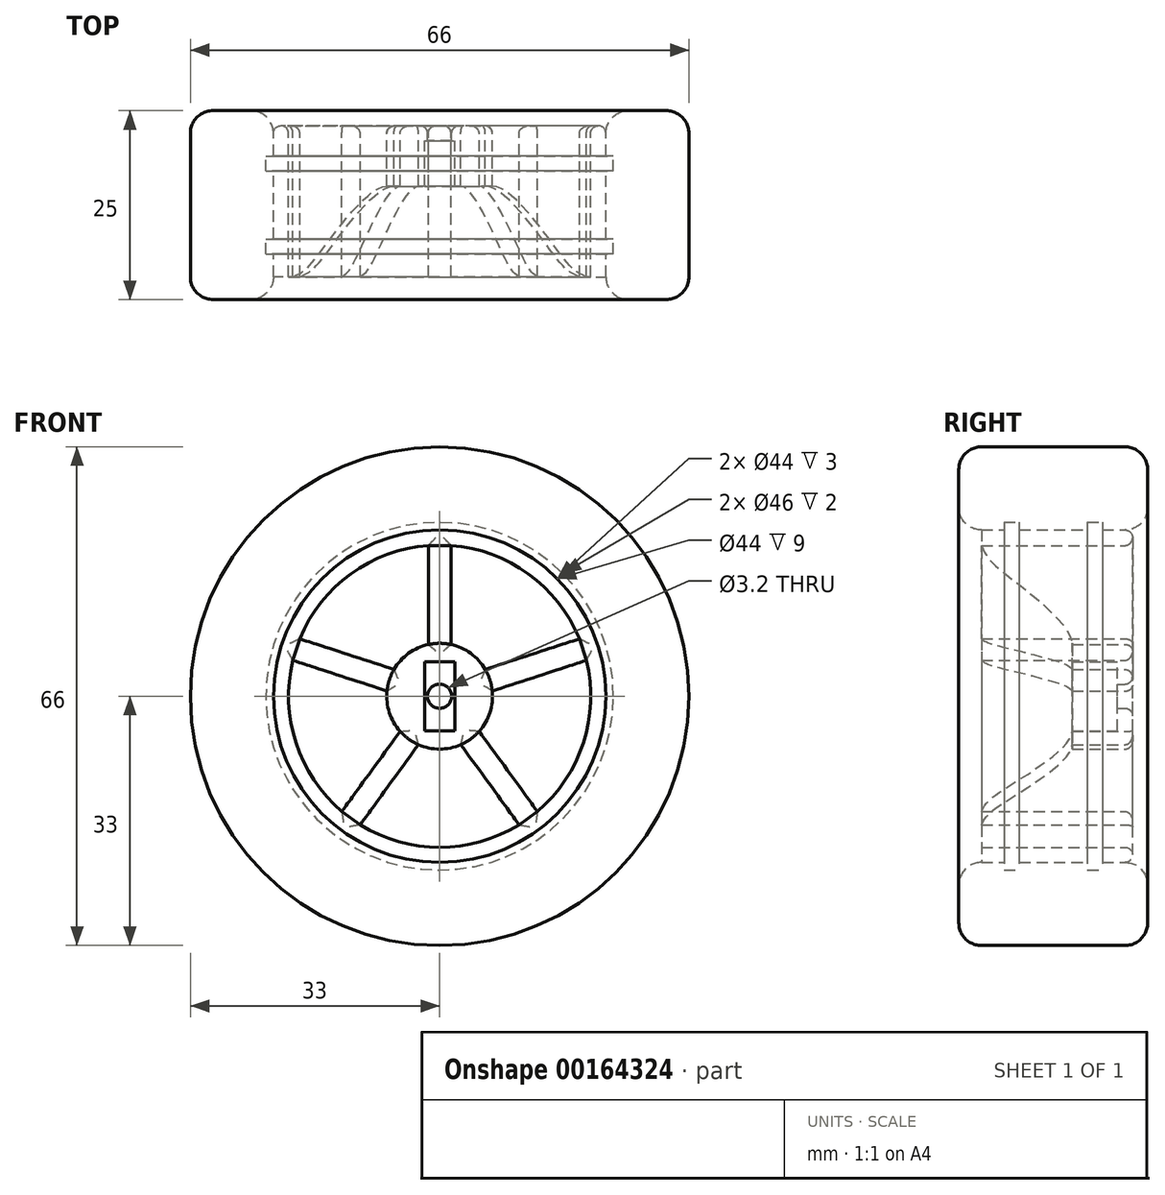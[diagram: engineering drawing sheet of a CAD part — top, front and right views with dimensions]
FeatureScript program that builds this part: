
annotation { "Feature Type Name" : "Feature", "Feature Type Description" : "" }
export const myFeature = defineFeature(function(context is Context, id is Id, definition is map)
    precondition{}
    {
        {
            var Q0;
            Q0=qCreatedBy(makeId("Front.planeOp"),FACE);
            var sketch = newSketch(context, id + "F0", { "sketchPlane" : qUnion([Q0])});
            skCircle(sketch, "E0", {"center": v(0, 0) * mm, "radius": 5 * mm, "construction": true});
            skCircle(sketch, "E1", {"center": v(0, 0) * mm, "radius": 22 * mm});
            skCircle(sketch, "E2.0", {"center": v(0, 0) * mm, "radius": 20 * mm});
            skCircle(sketch, "E3.0", {"center": v(0, 0) * mm, "radius": 7 * mm});
            skLineSegment(sketch, "E4.left", {"start": v(-1.5, 19.94) * mm, "end": v(-1.5, 6.84) * mm});
            skLineSegment(sketch, "E5.MirrorCS", {"start": v(1.5, 19.94) * mm, "end": v(1.5, 6.84) * mm});
            skLineSegment(sketch, "E6.bottom", {"start": v(-2, -4.58) * mm, "end": v(2, -4.58) * mm});
            skLineSegment(sketch, "E6.top", {"start": v(-2, 4.58) * mm, "end": v(2, 4.58) * mm});
            skLineSegment(sketch, "E6.left", {"start": v(-2, -4.58) * mm, "end": v(-2, 4.58) * mm});
            skLineSegment(sketch, "E6.right", {"start": v(2, -4.58) * mm, "end": v(2, 4.58) * mm});
            skCircle(sketch, "E7", {"center": v(0, 0) * mm, "radius": 1.6 * mm});
            skSolve(sketch);
        }
        {
            var Q0;
            Q0=makeQuery(id+"F0.imprint","IMPRINT",FACE,{"disambiguationData":[TD([[makeQuery(id+"F0.imprint","IMPRINT",EDGE,{"derivedFrom":sQuery(id+"F0.wireOp",EDGE,"E1")}),1.0]])]});
            extrude(context, id + "F1", {"entities" : qUnion([Q0]), "depth" : 20 * mm});
        }
        {
            var Q0;
            {var subQ0=sQuery(id+"F0.wireOp",EDGE,"E4.left");Q0=makeQuery(id+"F0.imprint","IMPRINT",FACE,{"disambiguationData":[TD([[makeQuery(id+"F0.imprint","IMPRINT",EDGE,{"derivedFrom":subQ0}),1.0]])]});}
            extrude(context, id + "F2", {"entities" : qUnion([Q0]), "depth" : 8 * mm});
        }
        {
            var Q0;
            Q0=makeQuery(id+"F0.imprint","IMPRINT",FACE,{"disambiguationData":[TD([[makeQuery(id+"F0.imprint","IMPRINT",EDGE,{"derivedFrom":sQuery(id+"F0.wireOp",EDGE,"E6.bottom")}),-1.0]])]});
            extrude(context, id + "F3", {"entities" : qUnion([Q0]), "operationType" : NewBodyOperationType.ADD, "depth" : 8 * mm, "hasSecondDirection" : true, "secondDirectionOppositeDirection" : false, "secondDirectionDepth" : 2 * mm});
        }
        {
            var Q0;
            Q0=makeQuery(id+"F0.imprint","IMPRINT",FACE,{"disambiguationData":[TD([[makeQuery(id+"F0.imprint","IMPRINT",EDGE,{"derivedFrom":sQuery(id+"F0.wireOp",EDGE,"E6.bottom")}),-1.0]])]});
            var Q1;
            Q1=makeQuery(id+"F0.imprint","IMPRINT",FACE,{"disambiguationData":[TD([[makeQuery(id+"F0.imprint","IMPRINT",EDGE,{"derivedFrom":sQuery(id+"F0.wireOp",EDGE,"E6.bottom")}),1.0]])]});
            extrude(context, id + "F4", {"entities" : qUnion([Q0, Q1]), "operationType" : NewBodyOperationType.ADD, "depth" : 2 * mm});
        }
        {
            var Q0;
            {var subQ0=sQuery(id+"F0.wireOp",EDGE,"E4.left");Q0=makeQuery(id+"F0.imprint","IMPRINT",FACE,{"disambiguationData":[TD([[makeQuery(id+"F0.imprint","IMPRINT",EDGE,{"derivedFrom":subQ0}),1.0]])]});}
            var Q1;
            Q1=makeQuery(id+"F1.opExtrude","CAP_FACE",FACE,{"disambiguationData":[OSD([sQuery(id+"F0.wireOp",EDGE,"E1"),sQuery(id+"F0.wireOp",EDGE,"E2.0")])],"isStart":false});
            extrude(context, id + "F5", {"entities" : qUnion([Q0]), "endBound" : BoundingType.UP_TO_SURFACE, "endBoundEntityFace" : qUnion([Q1]), "depth" : 25 * mm});
        }
        {
            var Q0;
            Q0=makeQuery(id+"F5.opExtrude","SWEPT_FACE",FACE,{"disambiguationData":[OSD([sQuery(id+"F0.wireOp",EDGE,"E5.MirrorCS")])]});
            var sketch = newSketch(context, id + "F6", { "sketchPlane" : qUnion([Q0])});
            skFitSpline(sketch, "E8", {"points": [v(-20, 19.94) * mm, v(-17.65, 16.85) * mm, v(-8, 6.84) * mm], "startDerivative": vector(5.52, -12.2) * mm, "endDerivative": vector(0, -13.55) * mm});
            skSolve(sketch);
        }
        {
            var Q0;
            {var subQ0=sQuery(id+"F6.wireOp",EDGE,"E8");Q0=makeQuery(id+"F6.imprint","IMPRINT",FACE,{"disambiguationData":[TD([[makeQuery(id+"F6.imprint","IMPRINT",EDGE,{"derivedFrom":subQ0}),-1.0]])]});}
            extrude(context, id + "F7", {"entities" : qUnion([Q0]), "operationType" : NewBodyOperationType.REMOVE, "endBound" : BoundingType.UP_TO_NEXT, "oppositeDirection" : true, "depth" : 25 * mm});
        }
        {
            var Q0;
            Q0=makeQuery(id+"F5.opExtrude","SWEPT_BODY",BODY,{"disambiguationData":[OSD([sQuery(id+"F0.wireOp",EDGE,"E2.0"),sQuery(id+"F0.wireOp",EDGE,"E3.0"),sQuery(id+"F0.wireOp",EDGE,"E4.left"),sQuery(id+"F0.wireOp",EDGE,"E5.MirrorCS")])]});
            var Q1;
            Q1=sQuery(id+"F0.wireOp",EDGE,"E0");
            circularPattern(context, id + "F8", {"entities" : qUnion([Q0]), "axis" : qUnion([Q1]), "angle" : 360 * degree, "instanceCount" : 5, "equalSpace" : true});
        }
        {
            var Q0;
            Q0=makeQuery(id+"F1.opExtrude","SWEPT_BODY",BODY,{"disambiguationData":[OSD([sQuery(id+"F0.wireOp",EDGE,"E1"),sQuery(id+"F0.wireOp",EDGE,"E2.0")])]});
            var Q1;
            Q1=makeQuery(id+"F2.opExtrude","SWEPT_BODY",BODY,{"disambiguationData":[OSD([sQuery(id+"F0.wireOp",EDGE,"E0"),sQuery(id+"F0.wireOp",EDGE,"E3.0")])]});
            var Q2;
            Q2=makeQuery(id+"F5.opExtrude","SWEPT_BODY",BODY,{"disambiguationData":[OSD([sQuery(id+"F0.wireOp",EDGE,"E2.0"),sQuery(id+"F0.wireOp",EDGE,"E3.0"),sQuery(id+"F0.wireOp",EDGE,"E4.left"),sQuery(id+"F0.wireOp",EDGE,"E5.MirrorCS")])]});
            var Q3;
            Q3=makeQuery(id+"F8.opPattern","COPY",BODY,{"derivedFrom":makeQuery(id+"F5.opExtrude","SWEPT_BODY",BODY,{"disambiguationData":[OSD([sQuery(id+"F0.wireOp",EDGE,"E2.0"),sQuery(id+"F0.wireOp",EDGE,"E3.0"),sQuery(id+"F0.wireOp",EDGE,"E4.left"),sQuery(id+"F0.wireOp",EDGE,"E5.MirrorCS")])]}),"instanceName":"1"});
            var Q4;
            Q4=makeQuery(id+"F8.opPattern","COPY",BODY,{"derivedFrom":makeQuery(id+"F5.opExtrude","SWEPT_BODY",BODY,{"disambiguationData":[OSD([sQuery(id+"F0.wireOp",EDGE,"E2.0"),sQuery(id+"F0.wireOp",EDGE,"E3.0"),sQuery(id+"F0.wireOp",EDGE,"E4.left"),sQuery(id+"F0.wireOp",EDGE,"E5.MirrorCS")])]}),"instanceName":"2"});
            var Q5;
            Q5=makeQuery(id+"F8.opPattern","COPY",BODY,{"derivedFrom":makeQuery(id+"F5.opExtrude","SWEPT_BODY",BODY,{"disambiguationData":[OSD([sQuery(id+"F0.wireOp",EDGE,"E2.0"),sQuery(id+"F0.wireOp",EDGE,"E3.0"),sQuery(id+"F0.wireOp",EDGE,"E4.left"),sQuery(id+"F0.wireOp",EDGE,"E5.MirrorCS")])]}),"instanceName":"3"});
            var Q6;
            Q6=makeQuery(id+"F8.opPattern","COPY",BODY,{"derivedFrom":makeQuery(id+"F5.opExtrude","SWEPT_BODY",BODY,{"disambiguationData":[OSD([sQuery(id+"F0.wireOp",EDGE,"E2.0"),sQuery(id+"F0.wireOp",EDGE,"E3.0"),sQuery(id+"F0.wireOp",EDGE,"E4.left"),sQuery(id+"F0.wireOp",EDGE,"E5.MirrorCS")])]}),"instanceName":"4"});
            booleanBodies(context, id + "F9", {"operationType" : BooleanOperationType.UNION, "tools" : qUnion([Q0, Q1, Q2, Q3, Q4, Q5, Q6])});
        }
        {
            var Q0;
            {var subQ0=sQuery(id+"F0.wireOp",EDGE,"E3.0");var subQ1=sQuery(id+"F0.wireOp",EDGE,"E2.0");var subQ2=makeQuery(id+"F5.opExtrude","CAP_FACE",FACE,{"disambiguationData":[OSD([subQ1,subQ0,sQuery(id+"F0.wireOp",EDGE,"E4.left"),sQuery(id+"F0.wireOp",EDGE,"E5.MirrorCS")])],"isStart":true});Q0=makeQuery(id+"F9.opBoolean","MERGE",FACE,{"derivedFrom":[makeQuery(id+"F1.opExtrude","CAP_FACE",FACE,{"disambiguationData":[OSD([sQuery(id+"F0.wireOp",EDGE,"E1"),subQ1])],"isStart":true}),makeQuery(id+"F2.opExtrude","CAP_FACE",FACE,{"disambiguationData":[OSD([sQuery(id+"F0.wireOp",EDGE,"E0"),subQ0])],"isStart":true}),subQ2,makeQuery(id+"F8.opPattern","COPY",FACE,{"derivedFrom":subQ2,"instanceName":"1"}),makeQuery(id+"F8.opPattern","COPY",FACE,{"derivedFrom":subQ2,"instanceName":"2"}),makeQuery(id+"F8.opPattern","COPY",FACE,{"derivedFrom":subQ2,"instanceName":"3"}),makeQuery(id+"F8.opPattern","COPY",FACE,{"derivedFrom":subQ2,"instanceName":"4"})]});}
            fillet(context, id + "F10", {"entities" : qUnion([Q0]), "radius" : 1 * mm, "tangentPropagation" : true, "allowEdgeOverflow" : false});
        }
        {
            var Q0;
            Q0=qCreatedBy(makeId("Right.planeOp"),FACE);
            var sketch = newSketch(context, id + "F11", { "sketchPlane" : qUnion([Q0])});
            skLineSegment(sketch, "E9", {"start": v(-20, 22) * mm, "end": v(-1, 22) * mm, "construction": true});
            skLineSegment(sketch, "E10", {"start": v(-1, -22) * mm, "end": v(-20, -22) * mm});
            skLineSegment(sketch, "E11.bottom", {"start": v(-6, 21) * mm, "end": v(-4, 21) * mm});
            skLineSegment(sketch, "E11.top", {"start": v(-6, 23) * mm, "end": v(-4, 23) * mm});
            skLineSegment(sketch, "E11.left", {"start": v(-6, 21) * mm, "end": v(-6, 23) * mm});
            skLineSegment(sketch, "E11.right", {"start": v(-4, 21) * mm, "end": v(-4, 23) * mm});
            skPoint(sketch, "E11.middle", {"position": v(-5, 22) * mm});
            skLineSegment(sketch, "E12", {"start": v(-10.5, 22) * mm, "end": v(-10.5, 25.44) * mm, "construction": true});
            skLineSegment(sketch, "E13.MirrorCS", {"start": v(-15, 23) * mm, "end": v(-17, 23) * mm});
            skLineSegment(sketch, "E14.MirrorCS", {"start": v(-15, 21) * mm, "end": v(-15, 23) * mm});
            skLineSegment(sketch, "E15.MirrorCS", {"start": v(-17, 21) * mm, "end": v(-17, 23) * mm});
            skLineSegment(sketch, "E16.MirrorCS", {"start": v(-15, 21) * mm, "end": v(-17, 21) * mm});
            skSolve(sketch);
        }
        {
            var Q0;
            Q0=makeQuery(id+"F11.imprint","IMPRINT",FACE,{"disambiguationData":[TD([[makeQuery(id+"F11.imprint","IMPRINT",EDGE,{"derivedFrom":sQuery(id+"F11.wireOp",EDGE,"E11.bottom")}),1.0]])]});
            var Q1;
            Q1=makeQuery(id+"F11.imprint","IMPRINT",FACE,{"disambiguationData":[TD([[makeQuery(id+"F11.imprint","IMPRINT",EDGE,{"derivedFrom":sQuery(id+"F11.wireOp",EDGE,"E13.MirrorCS")}),1.0]])]});
            var Q2;
            Q2=sQuery(id+"F0.wireOp",EDGE,"E0");
            revolve(context, id + "F12", {"operationType" : NewBodyOperationType.ADD, "entities" : qUnion([Q0, Q1]), "axis" : qUnion([Q2]), "revolveType" : RevolveType.FULL});
        }
        {
            var Q0;
            Q0=qCreatedBy(makeId("Right.planeOp"),FACE);
            var sketch = newSketch(context, id + "F13", { "sketchPlane" : qUnion([Q0])});
            skLineSegment(sketch, "E17", {"start": v(-15, 22) * mm, "end": v(-6, 22) * mm, "construction": true});
            skLineSegment(sketch, "E18", {"start": v(-6, -22) * mm, "end": v(-15, -22) * mm, "construction": true});
            skLineSegment(sketch, "E19", {"start": v(-10.5, 22) * mm, "end": v(-10.5, 33) * mm, "construction": true});
            skLineSegment(sketch, "E20.bottom", {"start": v(-20, 22) * mm, "end": v(-1, 22) * mm});
            skLineSegment(sketch, "E20.top", {"start": v(-20, 33) * mm, "end": v(-1, 33) * mm});
            skLineSegment(sketch, "E20.left", {"start": v(-23, 25) * mm, "end": v(-23, 30) * mm});
            skLineSegment(sketch, "E20.right", {"start": v(2, 25) * mm, "end": v(2, 30) * mm});
            skPoint(sketch, "E20.middle", {"position": v(-10.5, 27.5) * mm});
            skPoint(sketch, "E21.visualSharp", {"position": v(2, 33) * mm});
            skArc(sketch, "E21.filletArc", {"start": v(2, 30) * mm, "mid": v(1.12, 32.12) * mm, "end": v(-1, 33) * mm});
            skPoint(sketch, "E22.visualSharp", {"position": v(2, 22) * mm});
            skArc(sketch, "E22.filletArc", {"start": v(-1, 22) * mm, "mid": v(1.12, 22.88) * mm, "end": v(2, 25) * mm});
            skPoint(sketch, "E23.visualSharp", {"position": v(-23, 33) * mm});
            skArc(sketch, "E23.filletArc", {"start": v(-20, 33) * mm, "mid": v(-22.12, 32.12) * mm, "end": v(-23, 30) * mm});
            skPoint(sketch, "E24.visualSharp", {"position": v(-23, 22) * mm});
            skArc(sketch, "E24.filletArc", {"start": v(-23, 25) * mm, "mid": v(-22.12, 22.88) * mm, "end": v(-20, 22) * mm});
            skSolve(sketch);
        }
        {
            var Q0;
            Q0=makeQuery(id+"F13.imprint","IMPRINT",FACE,{"disambiguationData":[TD([[makeQuery(id+"F13.imprint","IMPRINT",EDGE,{"derivedFrom":sQuery(id+"F13.wireOp",EDGE,"E20.bottom")}),1.0]])]});
            var Q1;
            Q1=sQuery(id+"F0.wireOp",EDGE,"E0");
            revolve(context, id + "F14", {"entities" : qUnion([Q0]), "axis" : qUnion([Q1]), "revolveType" : RevolveType.FULL});
        }
        {
            var Q0;
            Q0=makeQuery(id+"F1.opExtrude","SWEPT_BODY",BODY,{"disambiguationData":[OSD([sQuery(id+"F0.wireOp",EDGE,"E1"),sQuery(id+"F0.wireOp",EDGE,"E2.0")])]});
            var Q1;
            Q1=makeQuery(id+"F14.opRevolve","SWEPT_BODY",BODY,{"disambiguationData":[OSD([sQuery(id+"F13.wireOp",EDGE,"E20.bottom"),sQuery(id+"F13.wireOp",EDGE,"E20.top"),sQuery(id+"F13.wireOp",EDGE,"E20.left"),sQuery(id+"F13.wireOp",EDGE,"E20.right"),sQuery(id+"F13.wireOp",EDGE,"E21.filletArc"),sQuery(id+"F13.wireOp",EDGE,"E22.filletArc"),sQuery(id+"F13.wireOp",EDGE,"E23.filletArc"),sQuery(id+"F13.wireOp",EDGE,"E24.filletArc")])]});
            booleanBodies(context, id + "F15", {"operationType" : BooleanOperationType.SUBTRACTION, "tools" : qUnion([Q0]), "targets" : qUnion([Q1]), "keepTools" : true});
        }
    });
